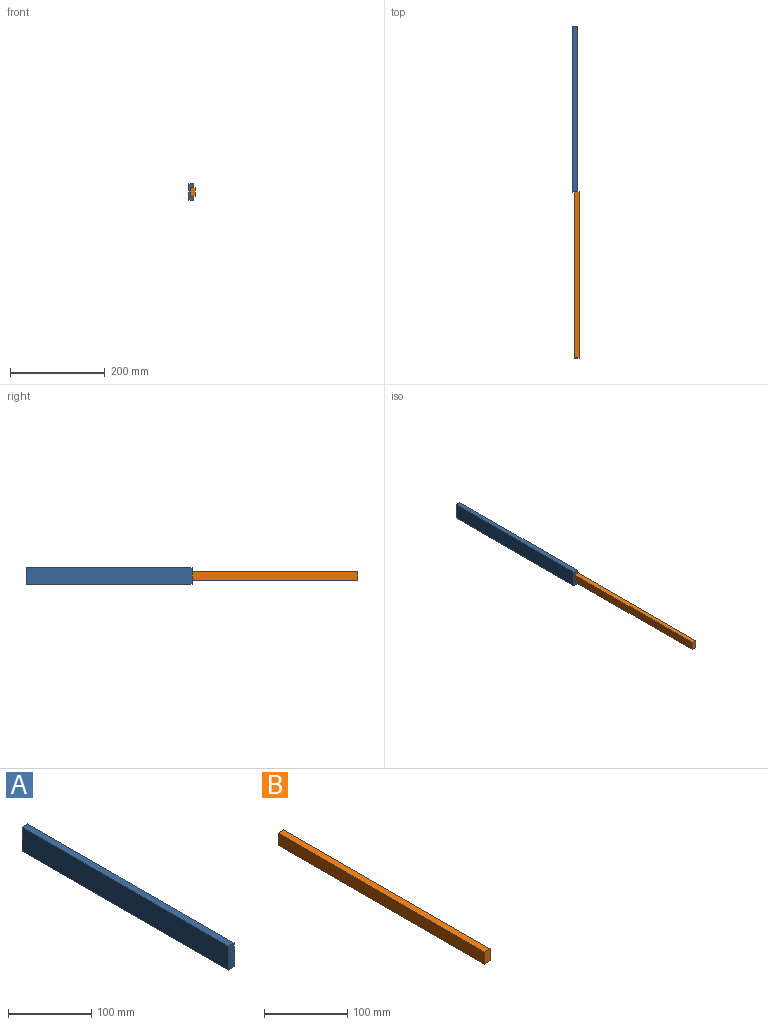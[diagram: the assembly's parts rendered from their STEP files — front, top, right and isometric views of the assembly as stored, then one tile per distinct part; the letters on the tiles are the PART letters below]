
ASSEMBLY  parts=2 mates=1
PART A: 6 faces, bbox 10x350x35 mm
  f0: plane 35x10mm, normal (0,-1,0), area 350mm2, adj f1,f3,f4,f5
  f1: plane 350x10mm, normal (0,0,-1), area 3500mm2, adj f0,f2,f4,f5
  f2: plane 35x10mm, normal (0,1,0), area 350mm2, adj f1,f3,f4,f5
  f3: plane 350x10mm, normal (0,0,1), area 3500mm2, adj f0,f2,f4,f5
  f4: plane 350x35mm, normal (1,0,0), area 12250mm2, adj f0,f1,f2,f3
  f5: plane 350x35mm, normal (-1,0,0), area 12250mm2, adj f0,f1,f2,f3
PART B: 6 faces, bbox 10x350x17.7 mm
  f0: plane 17.72x10mm, normal (0,1,0), area 177.2mm2, adj f1,f3,f4,f5
  f1: plane 350x10mm, normal (0,0,1), area 3500mm2, adj f0,f2,f4,f5
  f2: plane 17.72x10mm, normal (0,-1,0), area 177.2mm2, adj f1,f3,f4,f5
  f3: plane 350x10mm, normal (0,0,-1), area 3500mm2, adj f0,f2,f4,f5
  f4: plane 350x17.72mm, normal (1,0,0), area 6202.6mm2, adj f0,f1,f2,f3
  f5: plane 350x17.72mm, normal (-1,0,0), area 6202.6mm2, adj f0,f1,f2,f3
PLACE A at identity fixed
PLACE B at identity
MATE slider B.f0 <-> A.f0  axis (0,-1,0) through (5,-175,17.5)mm
